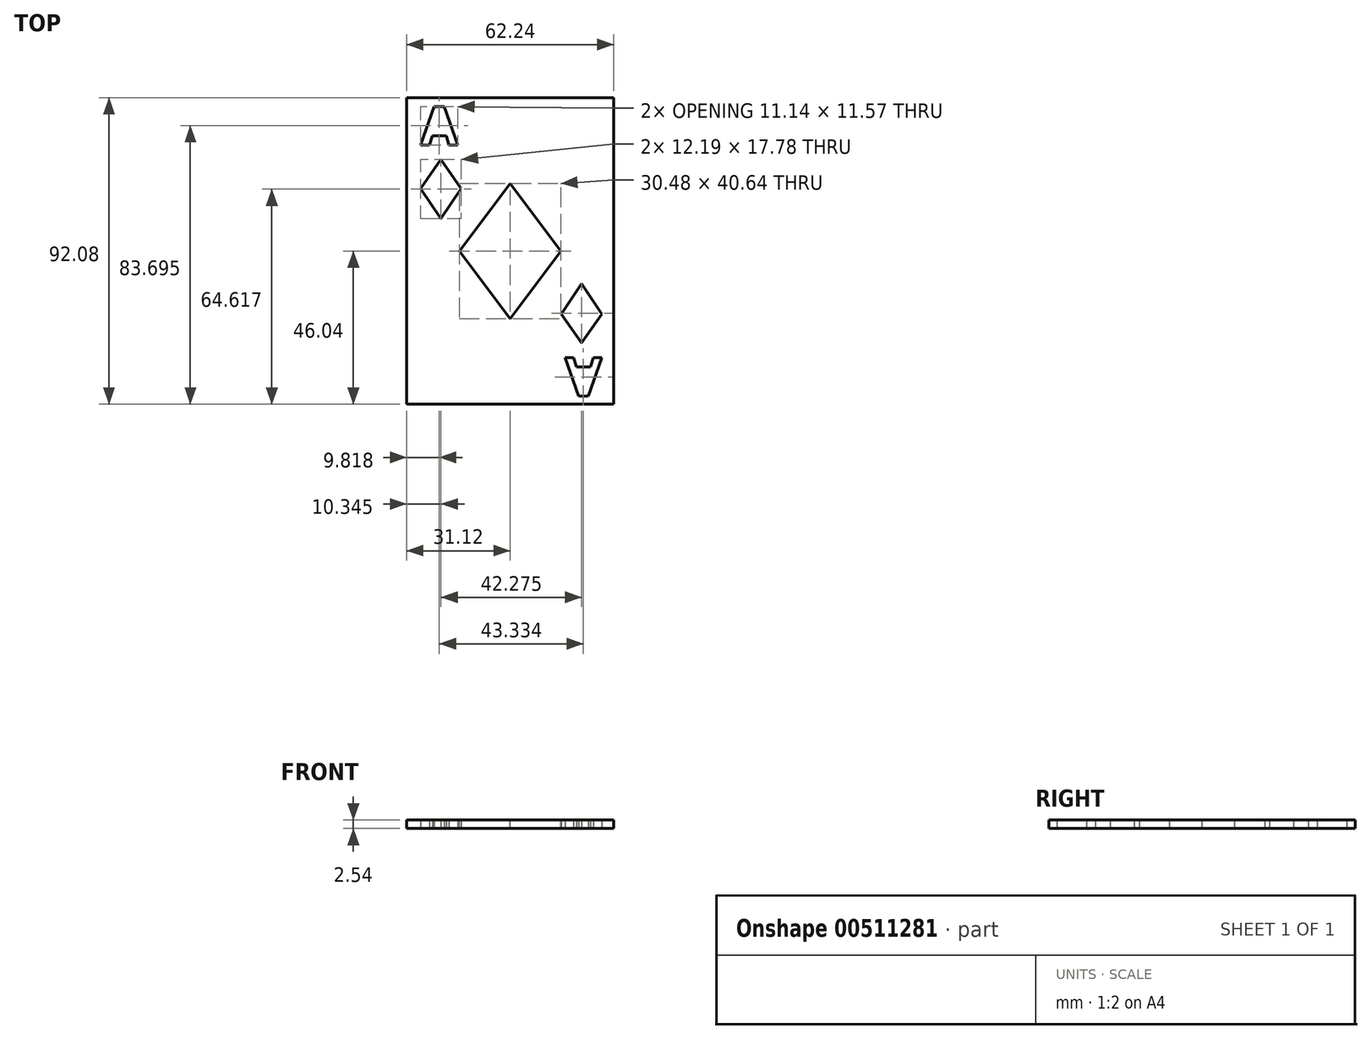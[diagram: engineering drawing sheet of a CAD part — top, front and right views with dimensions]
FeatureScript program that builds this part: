
annotation { "Feature Type Name" : "Feature", "Feature Type Description" : "" }
export const myFeature = defineFeature(function(context is Context, id is Id, definition is map)
    precondition{}
    {
        {
            var Q0;
            Q0=qCreatedBy(makeId("Top.planeOp"),FACE);
            var sketch = newSketch(context, id + "F0", { "sketchPlane" : qUnion([Q0])});
            skLineSegment(sketch, "E0.bottom", {"start": v(31.12, -46.04) * mm, "end": v(-31.12, -46.04) * mm});
            skLineSegment(sketch, "E0.top", {"start": v(31.12, 46.04) * mm, "end": v(-31.12, 46.04) * mm});
            skLineSegment(sketch, "E0.left", {"start": v(31.12, -46.04) * mm, "end": v(31.12, 46.04) * mm});
            skLineSegment(sketch, "E0.right", {"start": v(-31.12, -46.04) * mm, "end": v(-31.12, 46.04) * mm});
            skPoint(sketch, "E0.middle", {"position": v(0, 0) * mm});
            skText(sketch, "E1", { "text": "A", "fontName": "OpenSans-Bold.ttf"});
            skLineSegment(sketch, "E2", {"start": v(15.4, -18.95) * mm, "end": v(21.5, -27.65) * mm});
            skLineSegment(sketch, "E3", {"start": v(27.6, -18.95) * mm, "end": v(21.5, -27.65) * mm});
            skLineSegment(sketch, "E4", {"start": v(27.6, -18.95) * mm, "end": v(21.5, -9.87) * mm});
            skLineSegment(sketch, "E5", {"start": v(21.5, -9.87) * mm, "end": v(15.4, -18.95) * mm});
            skPoint(sketch, "E6", {"position": v(21.5, -18.76) * mm});
            skLineSegment(sketch, "E7", {"start": v(27.6, -18.95) * mm, "end": v(21.5, -18.76) * mm});
            skLineSegment(sketch, "E8", {"start": v(21.5, -18.76) * mm, "end": v(15.4, -18.95) * mm});
            skLineSegment(sketch, "E9", {"start": v(21.5, -27.65) * mm, "end": v(21.5, -18.76) * mm});
            skLineSegment(sketch, "E10", {"start": v(21.5, -18.76) * mm, "end": v(21.5, -9.87) * mm});
            skText(sketch, "E11", { "text": "A", "fontName": "OpenSans-Bold.ttf"});
            skLineSegment(sketch, "E12", {"start": v(-14.68, 18.78) * mm, "end": v(-20.77, 27.47) * mm});
            skLineSegment(sketch, "E13", {"start": v(-26.87, 18.77) * mm, "end": v(-20.77, 27.47) * mm});
            skLineSegment(sketch, "E14", {"start": v(-26.87, 18.77) * mm, "end": v(-20.77, 9.69) * mm});
            skLineSegment(sketch, "E15", {"start": v(-20.77, 9.69) * mm, "end": v(-14.68, 18.78) * mm});
            const initialGuessF0  = {"E1": [0.0276, -0.03205, -1, 0, 0.01162], "E11": [-0.02687, 0.03187, 1, 0, 0.01162]};
            skSetInitialGuess(sketch, initialGuessF0);
            skSolve(sketch);
        }
        {
            var Q0;
            Q0=makeQuery(id+"F0.imprint","IMPRINT",FACE,{"disambiguationData":[TD([[makeQuery(id+"F0.imprint","IMPRINT",EDGE,{"derivedFrom":sQuery(id+"F0.wireOp",EDGE,"E0.bottom")}),-1.0]])]});
            extrude(context, id + "F1", {"entities" : qUnion([Q0]), "depth" : 2.54 * mm, "offsetDistance" : 25.4 * mm});
        }
        {
            var Q0;
            Q0=makeQuery(id+"F1.opExtrude","CAP_FACE",FACE,{"disambiguationData":[OSD([sQuery(id+"F0.wireOp",EDGE,"E0.bottom"),sQuery(id+"F0.wireOp",EDGE,"E0.top"),sQuery(id+"F0.wireOp",EDGE,"E0.left"),sQuery(id+"F0.wireOp",EDGE,"E0.right"),sQuery(id+"F0.wireOp",EDGE,"8035d261-c012-438b-ab92-e9b7b63b235c.sketch_text.stroke-0"),sQuery(id+"F0.wireOp",EDGE,"8035d261-c012-438b-ab92-e9b7b63b235c.sketch_text.stroke-1"),sQuery(id+"F0.wireOp",EDGE,"8035d261-c012-438b-ab92-e9b7b63b235c.sketch_text.stroke-2"),sQuery(id+"F0.wireOp",EDGE,"8035d261-c012-438b-ab92-e9b7b63b235c.sketch_text.stroke-3"),sQuery(id+"F0.wireOp",EDGE,"8035d261-c012-438b-ab92-e9b7b63b235c.sketch_text.stroke-4"),sQuery(id+"F0.wireOp",EDGE,"8035d261-c012-438b-ab92-e9b7b63b235c.sketch_text.stroke-5"),sQuery(id+"F0.wireOp",EDGE,"8035d261-c012-438b-ab92-e9b7b63b235c.sketch_text.stroke-6"),sQuery(id+"F0.wireOp",EDGE,"8035d261-c012-438b-ab92-e9b7b63b235c.sketch_text.stroke-7"),sQuery(id+"F0.wireOp",EDGE,"E1.sketch_text.stroke-0"),sQuery(id+"F0.wireOp",EDGE,"E1.sketch_text.stroke-1"),sQuery(id+"F0.wireOp",EDGE,"E1.sketch_text.stroke-2"),sQuery(id+"F0.wireOp",EDGE,"E1.sketch_text.stroke-3"),sQuery(id+"F0.wireOp",EDGE,"E1.sketch_text.stroke-4"),sQuery(id+"F0.wireOp",EDGE,"E1.sketch_text.stroke-5"),sQuery(id+"F0.wireOp",EDGE,"E1.sketch_text.stroke-6"),sQuery(id+"F0.wireOp",EDGE,"E1.sketch_text.stroke-7"),sQuery(id+"F0.wireOp",EDGE,"E2"),sQuery(id+"F0.wireOp",EDGE,"E3"),sQuery(id+"F0.wireOp",EDGE,"E4"),sQuery(id+"F0.wireOp",EDGE,"E5"),sQuery(id+"F0.wireOp",EDGE,"5e8ebfa5-02f0-443d-b341-d0c3b3ca4b14"),sQuery(id+"F0.wireOp",EDGE,"c2504083-f707-4154-b1b5-35a5d9cb9918"),sQuery(id+"F0.wireOp",EDGE,"b4d9873e-e40f-499a-8181-8d0fc2a8ffb0"),sQuery(id+"F0.wireOp",EDGE,"4a4fa5f1-679d-400a-8557-fc44a12dfce8")])],"isStart":false});
            var sketch = newSketch(context, id + "F2", { "sketchPlane" : qUnion([Q0])});
            skLineSegment(sketch, "E16", {"start": v(0, -20.32) * mm, "end": v(15.24, 0) * mm});
            skLineSegment(sketch, "E17", {"start": v(15.24, 0) * mm, "end": v(0, 20.32) * mm});
            skLineSegment(sketch, "E18", {"start": v(0, 20.32) * mm, "end": v(-15.24, 0) * mm});
            skLineSegment(sketch, "E19", {"start": v(-15.24, 0) * mm, "end": v(0, -20.32) * mm});
            skLineSegment(sketch, "E20", {"start": v(0, 0) * mm, "end": v(0, -20.32) * mm});
            skLineSegment(sketch, "E21", {"start": v(0, 0) * mm, "end": v(0, 20.32) * mm});
            skLineSegment(sketch, "E22", {"start": v(0, 0) * mm, "end": v(15.24, 0) * mm});
            skLineSegment(sketch, "E23", {"start": v(0, 0) * mm, "end": v(-15.24, 0) * mm});
            skSolve(sketch);
        }
        {
            var Q0;
            Q0 = qSketchRegion(id + "F2", true);
            extrude(context, id + "F3", {"entities" : qUnion([Q0]), "operationType" : NewBodyOperationType.REMOVE, "depth" : -12.7 * mm, "offsetDistance" : 25.4 * mm});
        }
    });
